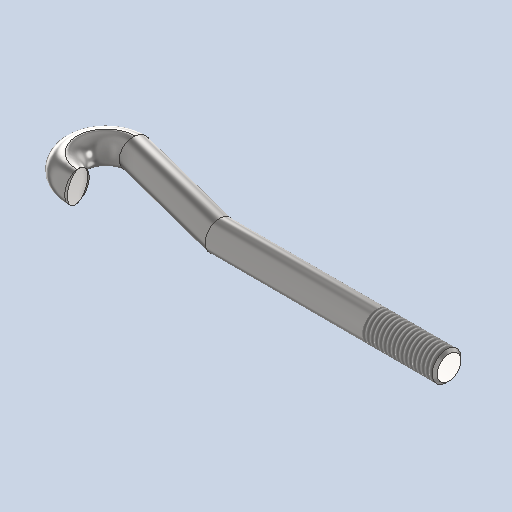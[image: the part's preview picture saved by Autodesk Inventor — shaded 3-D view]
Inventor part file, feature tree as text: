
AUTODESK INVENTOR PART (.ipt)
format: ipt  version: 2025 (Build 290162010, 162A)  size: 214,528 bytes
history: native  units: mm
features: other x3, extrude x1, sketch x1
ambient origin geometry x8: Origin, YZ Plane, XZ Plane, XY Plane, X Axis, Y Axis, Z Axis, Center Point
bodies: Solid1 (feature_tree)
feature tree (5):
  other  "DIN 529 M12 x 160"
  extrude  "Extrusion1"  Depth=5.5mm TaperAngle=0.0deg
  other  "Solid1::DIN 529 M12 x 160"
  other  "Bezeichnung1"
  sketch  "Skizze1"  dims[d0=2.5mm d1=5.5mm d2=0.0mm]
